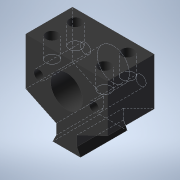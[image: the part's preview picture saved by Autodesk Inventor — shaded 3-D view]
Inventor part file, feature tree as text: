
AUTODESK INVENTOR PART (.ipt)
format: ipt  version: 2021 (Build 250183000, 183)  size: 141,824 bytes
history: native  units: mm
features: extrude x2, sketch x2
ambient origin geometry x8: Origin, YZ Plane, XZ Plane, XY Plane, X Axis, Y Axis, Z Axis, Center Point
bodies: Solid1 (feature_tree)
feature tree (4):
  extrude  "Extrusion1"  Depth=17.25mm
  extrude  "Extrusion2"  Depth=9.5mm
  sketch  "Sketch1"  dims[d0=11.0mm d1=17.25mm]
  sketch  "Sketch2"  dims[d2=7.0mm d3=9.5mm d4=11.070623mm d5=6.0mm d6=5.0mm d7=28.0mm d8=3.5mm d9=19.0mm d10=9.5mm d11=10.0mm d12=16.0mm d13=0.0mm d14=18.0mm d15=9.0mm d17=4.0mm d18=4.2mm d19=4.0mm d20=7.0mm d21=0.0mm]
